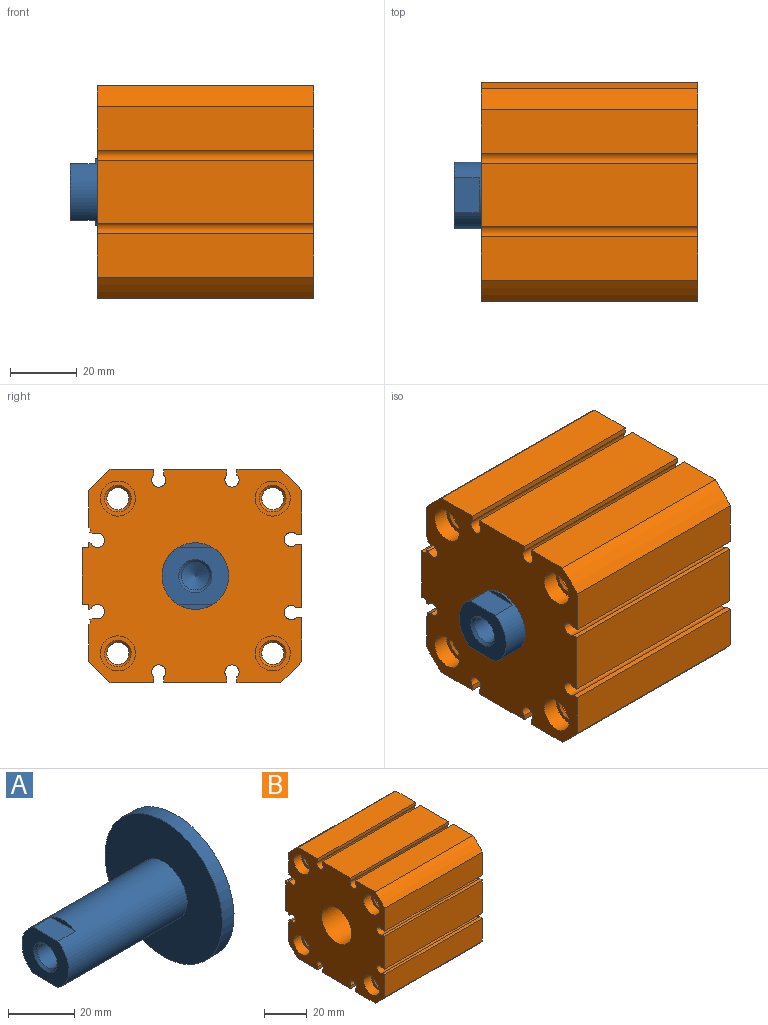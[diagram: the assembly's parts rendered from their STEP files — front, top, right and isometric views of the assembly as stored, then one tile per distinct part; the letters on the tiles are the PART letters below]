
ASSEMBLY  parts=2 mates=1
PART A: 12 faces, bbox 55.5x50x50 mm
  f0: plane 20x17mm, normal (-1,0,0), area 214.2mm2, adj f1,f4,f8,f9
  f1: cone r=4.19mm half-angle=45deg, axis (-1,0,0), area 33.1mm2, adj f0,f2
  f2: cylinder r=4.19mm len=15.19mm, axis (-1,0,0), area 399.7mm2, adj f1,f3
  f3: cone r=866.03mm half-angle=60deg, axis (-1,0,0), area 63.6mm2, adj f2
  f4: cylinder r=10mm len=50.5mm, axis (-1,0,0), area 3006.6mm2, adj f0,f5,f8,f9,f10,f11
  f5: plane 50x50mm, normal (-1,0,0), area 1649.3mm2, adj f4,f6
  f6: cylinder r=25mm len=50mm, axis (-1,0,0), area 785.4mm2, adj f5,f7
  f7: plane 50x50mm, normal (1,0,0), area 1963.5mm2, adj f6
  f8: plane 10.54x7.5mm, normal (0,0,1), area 79mm2, adj f0,f4,f10
  f9: plane 10.54x7.5mm, normal (0,0,-1), area 79mm2, adj f0,f4,f11
  f10: plane 10.54x1.5mm, normal (-1,0,0), area 10.7mm2, adj f4,f8
  f11: plane 10.54x1.5mm, normal (-1,0,0), area 10.7mm2, adj f4,f9
PART B: 104 faces, bbox 65x66x64 mm
  f0: cylinder r=41mm len=65mm, axis (1,0,0), area 586.6mm2, adj f1,f2,f3,f52
  f1: plane 66x64mm, normal (1,0,0), area 3557.3mm2, adj f0,f2,f3,f4,f5,f6,f7,f8
  f2: plane 65x11.03mm, normal (0,1,0), area 717.1mm2, adj f0,f1,f48,f52
  f3: plane 65x13.12mm, normal (0,0,1), area 852.9mm2, adj f0,f1,f4,f52
  f4: plane 65x1.71mm, normal (0,-1,0), area 110.8mm2, adj f1,f3,f5,f52
  f5: cylinder r=2.12mm len=65mm, axis (1,0,0), area 649.5mm2, adj f1,f4,f6,f52
  f6: plane 65x1.56mm, normal (0,1,0), area 101.1mm2, adj f1,f5,f7,f52
  f7: plane 65x18.98mm, normal (0,0,1), area 1233.7mm2, adj f1,f6,f8,f52
  f8: plane 65x1.56mm, normal (0,-1,0), area 101.1mm2, adj f1,f7,f9,f52
  f9: cylinder r=2.12mm len=65mm, axis (1,0,0), area 649.5mm2, adj f1,f8,f10,f52
  f10: plane 65x1.71mm, normal (0,1,0), area 110.8mm2, adj f1,f9,f11,f52
  f11: plane 65x13.12mm, normal (0,0,1), area 852.9mm2, adj f1,f10,f12,f52
  f12: cylinder r=41mm len=65mm, axis (1,0,0), area 586.6mm2, adj f1,f11,f13,f52
  f13: plane 65x13.12mm, normal (0,-1,0), area 852.9mm2, adj f1,f12,f14,f52
  f14: plane 65x1.71mm, normal (0,0,-1), area 110.8mm2, adj f1,f13,f15,f52
  f15: cylinder r=2.12mm len=65mm, axis (1,0,0), area 649.5mm2, adj f1,f14,f16,f52
  f16: plane 65x1.56mm, normal (0,0,1), area 101.1mm2, adj f1,f15,f17,f52
  f17: plane 65x18.98mm, normal (0,-1,0), area 1233.7mm2, adj f1,f16,f18,f52
  f18: plane 65x1.56mm, normal (0,0,-1), area 101.1mm2, adj f1,f17,f19,f52
  f19: cylinder r=2.12mm len=65mm, axis (1,0,0), area 649.5mm2, adj f1,f18,f20,f52
  f20: plane 65x1.71mm, normal (0,0,1), area 110.8mm2, adj f1,f19,f21,f52
  f21: plane 65x13.12mm, normal (0,-1,0), area 852.9mm2, adj f1,f20,f22,f52
  f22: cylinder r=41mm len=65mm, axis (1,0,0), area 586.6mm2, adj f1,f21,f23,f52
  f23: plane 65x13.12mm, normal (0,0,-1), area 852.9mm2, adj f1,f22,f24,f52
  f24: plane 65x1.71mm, normal (0,1,0), area 110.8mm2, adj f1,f23,f25,f52
  f25: cylinder r=2.12mm len=65mm, axis (1,0,0), area 649.5mm2, adj f1,f24,f26,f52
  f26: plane 65x1.56mm, normal (0,-1,0), area 101.1mm2, adj f1,f25,f27,f52
  f27: plane 65x18.98mm, normal (0,0,-1), area 1233.7mm2, adj f1,f26,f28,f52
  f28: plane 65x1.56mm, normal (0,1,0), area 101.1mm2, adj f1,f27,f29,f52
  f29: cylinder r=2.12mm len=65mm, axis (1,0,0), area 649.5mm2, adj f1,f28,f30,f52
  f30: plane 65x1.71mm, normal (0,-1,0), area 110.8mm2, adj f1,f29,f31,f52
  f31: plane 65x13.12mm, normal (0,0,-1), area 852.9mm2, adj f1,f30,f32,f52
  f32: cylinder r=41mm len=65mm, axis (1,0,0), area 586.6mm2, adj f1,f31,f33,f52
  f33: plane 65x11.03mm, normal (0,1,0), area 717.1mm2, adj f1,f32,f34,f52
  f34: plane 65x0.6mm, normal (0,0.71,0.71), area 55.2mm2, adj f1,f33,f35,f52
  f35: plane 65x0.85mm, normal (0,0.94,-0.34), area 58.9mm2, adj f1,f34,f36,f52
  f36: plane 65x1.42mm, normal (0,0.34,0.94), area 98.4mm2, adj f1,f35,f37,f52
  f37: cylinder r=2.12mm len=65mm, axis (1,0,0), area 649.5mm2, adj f1,f36,f38,f52
  f38: plane 65x0.68mm, normal (0,-0.34,-0.94), area 46.9mm2, adj f1,f37,f39,f52
  f39: plane 65x1.54mm, normal (0,1,0), area 100.1mm2, adj f1,f38,f40,f52
  f40: plane 65x2mm, normal (0,0,-1), area 130mm2, adj f1,f39,f41,f52
  f41: plane 65x17mm, normal (0,1,0), area 956.3mm2, adj f1,f40,f42,f50,f52,f53
  f42: plane 65x2mm, normal (0,0,1), area 130mm2, adj f1,f41,f43,f52
  f43: plane 65x1.54mm, normal (0,1,0), area 100.1mm2, adj f1,f42,f44,f52
  f44: plane 65x0.68mm, normal (0,-0.34,0.94), area 46.9mm2, adj f1,f43,f45,f52
  f45: cylinder r=2.12mm len=65mm, axis (1,0,0), area 650.5mm2, adj f1,f44,f46,f52
  f46: plane 65x1.41mm, normal (0,0.34,-0.94), area 97.7mm2, adj f1,f45,f47,f52
  f47: plane 65x0.86mm, normal (0,0.94,0.34), area 59.6mm2, adj f1,f46,f48,f52
  f48: plane 65x0.6mm, normal (0,0.71,-0.71), area 55.2mm2, adj f1,f2,f47,f52
  f49: cylinder r=4.28mm len=8.57mm, axis (0,-1,0), area 145.8mm2, adj f50,f51
  f50: cone r=4.28mm half-angle=45deg, axis (0,1,0), area 23.6mm2, adj f41,f49
  f51: cone r=866.03mm half-angle=60deg, axis (0,1,0), area 66.5mm2, adj f49
  f52: plane 66x64mm, normal (-1,0,0), area 3243.1mm2, adj f0,f2,f3,f4,f5,f6,f7,f8
  f53: cone r=4.28mm half-angle=45deg, axis (0,1,0), area 23.6mm2, adj f41,f55
  f54: cylinder r=5.25mm len=10.5mm, axis (-1,0,0), area 164.9mm2, adj f52,f57
  f55: cylinder r=4.28mm len=8.57mm, axis (0,-1,0), area 145.8mm2, adj f53,f56
  f56: cone r=866.03mm half-angle=60deg, axis (0,1,0), area 66.5mm2, adj f55
  f57: plane 10.5x10.5mm, normal (-1,0,0), area 36.3mm2, adj f54,f58
  f58: cone r=4mm half-angle=45deg, axis (-1,0,0), area 22mm2, adj f57,f59
  f59: cylinder r=3.32mm len=14.32mm, axis (-1,0,0), area 299.1mm2, adj f58,f60
  f60: plane 6.65x6.65mm, normal (-1,0,0), area 0.5mm2, adj f59,f61
  f61: cylinder r=3.3mm len=25mm, axis (-1,0,0), area 518.4mm2, adj f60,f62
  f62: plane 6.65x6.65mm, normal (1,0,0), area 0.5mm2, adj f61,f63
  f63: cylinder r=3.32mm len=14.32mm, axis (-1,0,0), area 299.1mm2, adj f62,f64
  f64: cone r=3.32mm half-angle=45deg, axis (1,0,0), area 22mm2, adj f63,f65
  f65: plane 10.5x10.5mm, normal (1,0,0), area 36.3mm2, adj f64,f66
  f66: cylinder r=5.25mm len=10.5mm, axis (-1,0,0), area 164.9mm2, adj f1,f65
  f67: cylinder r=5.25mm len=10.5mm, axis (-1,0,0), area 164.9mm2, adj f52,f68
  f68: plane 10.5x10.5mm, normal (-1,0,0), area 36.3mm2, adj f67,f69
  f69: cone r=4mm half-angle=45deg, axis (-1,0,0), area 22mm2, adj f68,f70
  f70: cylinder r=3.32mm len=14.32mm, axis (-1,0,0), area 299.1mm2, adj f69,f71
  f71: plane 6.65x6.65mm, normal (-1,0,0), area 0.5mm2, adj f70,f72
  f72: cylinder r=3.3mm len=25mm, axis (-1,0,0), area 518.4mm2, adj f71,f73
  f73: plane 6.65x6.65mm, normal (1,0,0), area 0.5mm2, adj f72,f74
  f74: cylinder r=3.32mm len=14.32mm, axis (-1,0,0), area 299.1mm2, adj f73,f75
  f75: cone r=3.32mm half-angle=45deg, axis (1,0,0), area 22mm2, adj f74,f76
  f76: plane 10.5x10.5mm, normal (1,0,0), area 36.3mm2, adj f75,f77
  f77: cylinder r=5.25mm len=10.5mm, axis (-1,0,0), area 164.9mm2, adj f1,f76
  f78: cylinder r=5.25mm len=10.5mm, axis (-1,0,0), area 164.9mm2, adj f52,f79
  f79: plane 10.5x10.5mm, normal (-1,0,0), area 36.3mm2, adj f78,f80
  f80: cone r=4mm half-angle=45deg, axis (-1,0,0), area 22mm2, adj f79,f81
  f81: cylinder r=3.32mm len=14.32mm, axis (-1,0,0), area 299.1mm2, adj f80,f82
  f82: plane 6.65x6.65mm, normal (-1,0,0), area 0.5mm2, adj f81,f83
  f83: cylinder r=3.3mm len=25mm, axis (-1,0,0), area 518.4mm2, adj f82,f84
  f84: plane 6.65x6.65mm, normal (1,0,0), area 0.5mm2, adj f83,f85
  f85: cylinder r=3.32mm len=14.32mm, axis (-1,0,0), area 299.1mm2, adj f84,f86
  f86: cone r=3.32mm half-angle=45deg, axis (1,0,0), area 22mm2, adj f85,f87
  f87: plane 10.5x10.5mm, normal (1,0,0), area 36.3mm2, adj f86,f88
  f88: cylinder r=5.25mm len=10.5mm, axis (-1,0,0), area 164.9mm2, adj f1,f87
  f89: cylinder r=5.25mm len=10.5mm, axis (-1,0,0), area 164.9mm2, adj f52,f90
  f90: plane 10.5x10.5mm, normal (-1,0,0), area 36.3mm2, adj f89,f91
  f91: cone r=4mm half-angle=45deg, axis (-1,0,0), area 22mm2, adj f90,f92
  f92: cylinder r=3.32mm len=14.32mm, axis (-1,0,0), area 299.1mm2, adj f91,f93
  f93: plane 6.65x6.65mm, normal (-1,0,0), area 0.5mm2, adj f92,f94
  f94: cylinder r=3.3mm len=25mm, axis (-1,0,0), area 518.4mm2, adj f93,f95
  f95: plane 6.65x6.65mm, normal (1,0,0), area 0.5mm2, adj f94,f96
  f96: cylinder r=3.32mm len=14.32mm, axis (-1,0,0), area 299.1mm2, adj f95,f97
  f97: cone r=3.32mm half-angle=45deg, axis (1,0,0), area 22mm2, adj f96,f98
  f98: plane 10.5x10.5mm, normal (1,0,0), area 36.3mm2, adj f97,f99
  f99: cylinder r=5.25mm len=10.5mm, axis (-1,0,0), area 164.9mm2, adj f1,f98
  f100: cylinder r=10mm len=22.5mm, axis (-1,0,0), area 1413.7mm2, adj f52,f101
  f101: plane 50x50mm, normal (1,0,0), area 1649.3mm2, adj f100,f102
  f102: cylinder r=25mm len=50mm, axis (-1,0,0), area 3927mm2, adj f101,f103
  f103: plane 50x50mm, normal (-1,0,0), area 1963.5mm2, adj f102
PLACE A t=(35.69,4.36,69.2)mm
PLACE B rot(axis=(-1,0,0),0deg) t=(35.81,4.36,69.2)mm
MATE slider B.f12 <-> A.f1  axis (-1,0,0) through (83.31,4.36,69.2)mm
